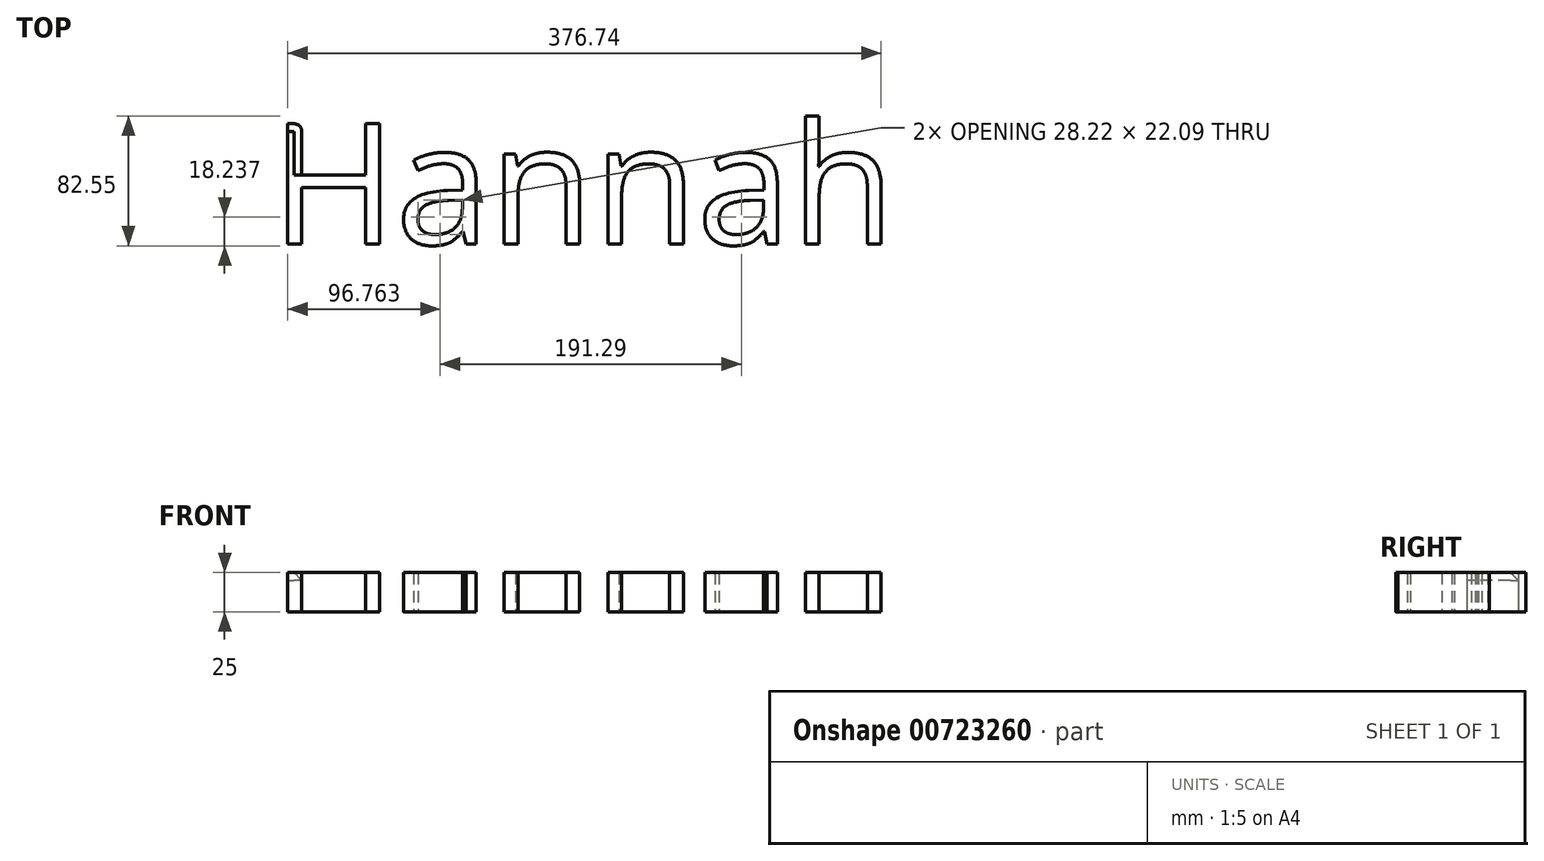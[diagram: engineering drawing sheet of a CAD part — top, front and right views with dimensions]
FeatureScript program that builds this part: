
annotation { "Feature Type Name" : "Feature", "Feature Type Description" : "" }
export const myFeature = defineFeature(function(context is Context, id is Id, definition is map)
    precondition{}
    {
        {
            var Q0;
            Q0=qCreatedBy(makeId("Top.planeOp"),FACE);
            var sketch = newSketch(context, id + "F0", { "sketchPlane" : qUnion([Q0])});
            skText(sketch, "E0", { "text": "Hannah", "fontName": "OpenSans-Regular.ttf"});
            const initialGuessF0  = {"E0": [-0.39422, -0.06052, 1, 0, 0.07722]};
            skSetInitialGuess(sketch, initialGuessF0);
            skSolve(sketch);
        }
        {
            var Q0;
            Q0 = qSketchRegion(id + "F0", true);
            extrude(context, id + "F1", {"entities" : qUnion([Q0]), "depth" : 25 * mm, "offsetDistance" : 25 * mm});
        }
        {
            var Q0;
            Q0=makeQuery(id+"F1.opExtrude","SWEPT_EDGE",EDGE,{"disambiguationData":[OSD([sQuery(id+"F0.wireOp",EDGE,"E0.sketch_text.stroke-6"),sQuery(id+"F0.wireOp",EDGE,"E0.sketch_text.stroke-7")])]});
            fillet(context, id + "F2", {"entities" : qUnion([Q0]), "radius" : 5 * mm, "tangentPropagation" : true, "allowEdgeOverflow" : false});
        }
        {
            var Q0;
            Q0=makeQuery(id+"F1.opExtrude","CAP_EDGE",EDGE,{"disambiguationData":[OSD([sQuery(id+"F0.wireOp",EDGE,"E0.sketch_text.stroke-7")])],"isStart":false});
            chamfer(context, id + "F3", {"entities" : qUnion([Q0]), "width" : 5 * mm, "tangentPropagation" : true});
        }
    });
